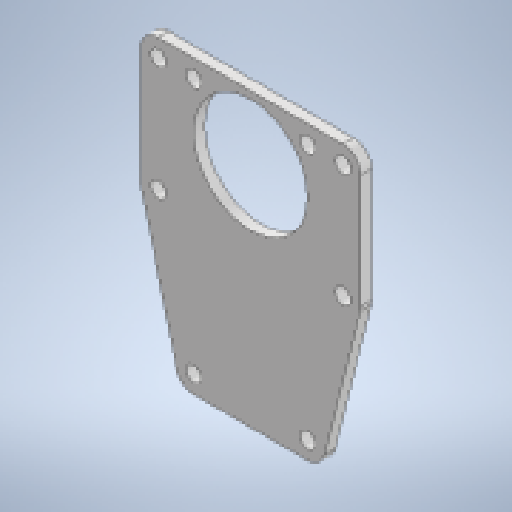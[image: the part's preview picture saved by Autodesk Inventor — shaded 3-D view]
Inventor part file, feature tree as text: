
AUTODESK INVENTOR PART (.ipt)
format: ipt  version: 2025.1 (Build 291241000, 241)  size: 262,144 bytes
history: native  units: mm
features: reference x17, other x9, extrude x2, sketch x2, fillet x1
ambient origin geometry x8: Origin, YZ Plane, XZ Plane, XY Plane, X Axis, Y Axis, Z Axis, Center Point
bodies: Body1 (feature_tree)
feature tree (31):
  other  "ソリッド1"
  extrude  "押し出し1"  Depth=2.2mm
  extrude  "押し出し2"  Depth=2.2mm
  fillet  "フィレット1"  Radius=2.2mm
  sketch  "スケッチ1"
  reference  "参照1"
  reference  "参照2"
  reference  "参照3"
  reference  "参照4"
  reference  "参照5"
  reference  "参照6"
  reference  "参照7"
  reference  "参照8"
  sketch  "スケッチ2"
  reference  "参照9"
  reference  "参照10"
  reference  "参照11"
  reference  "参照12"
  reference  "参照13"
  reference  "参照14"
  reference  "参照15"
  reference  "参照16"
  reference  "参照17"
  other  "<userpath>\Documents\Inventor\Vixen\kosi_v2.iam"
  other  "kosi_v2.iam"
  other  "KRS2500_scale:7"
  other  "KRS2500_scale:5"
  other  "KRS2500_scale:6"
  other  "02157_SmallDiameterHornB:3"
  other  "02159_SmallFreeHornC:2"
  other  "02159_SmallFreeHornC:3"
